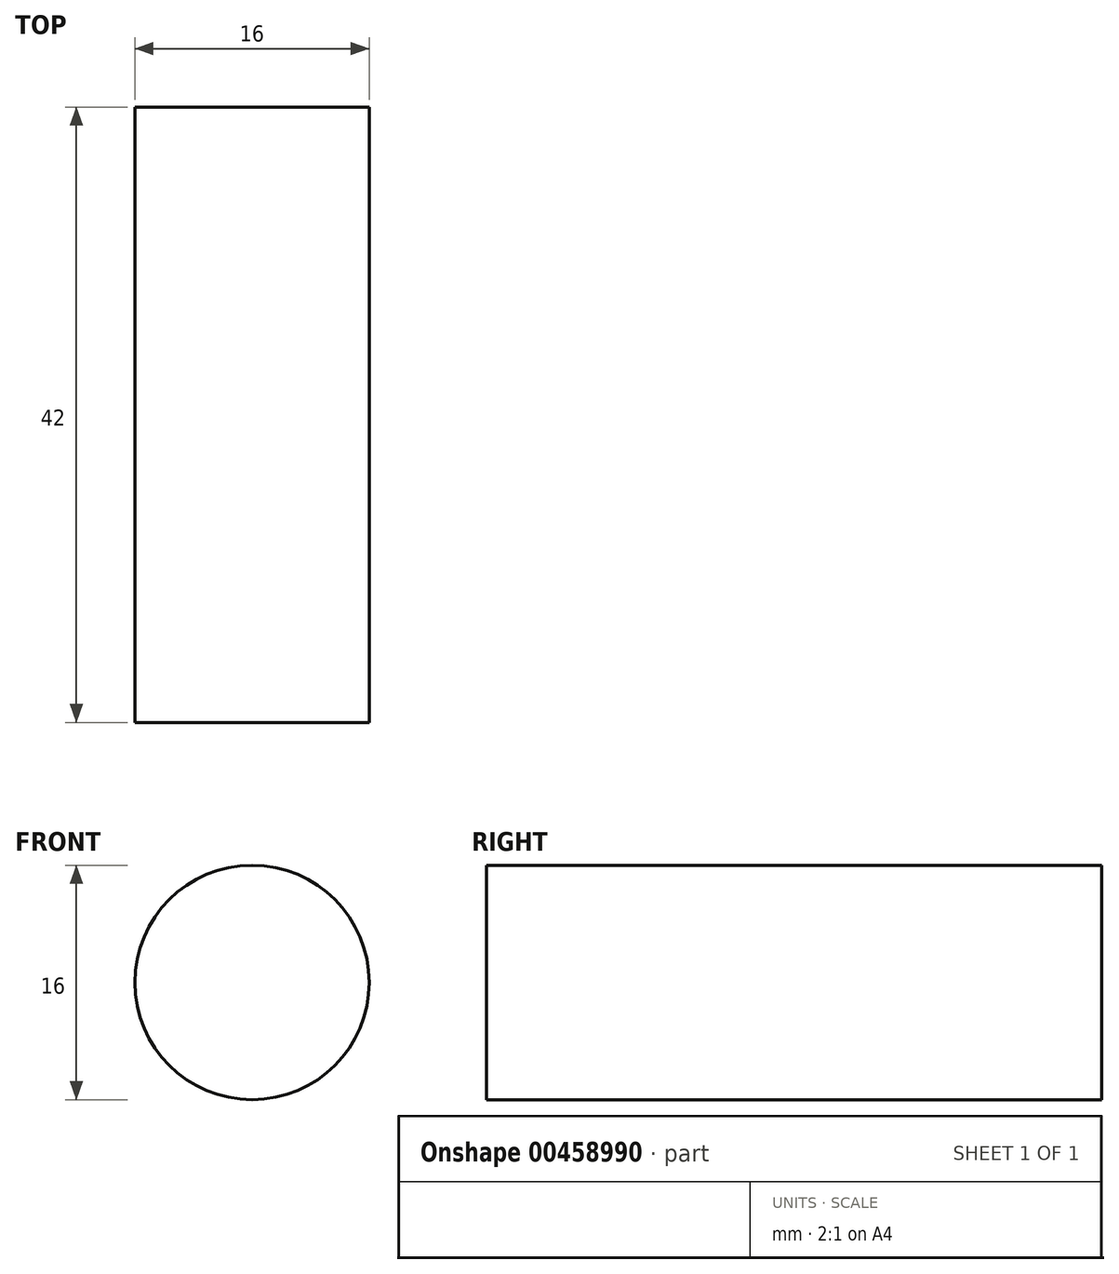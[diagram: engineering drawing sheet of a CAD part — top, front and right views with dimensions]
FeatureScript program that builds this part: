
annotation { "Feature Type Name" : "Feature", "Feature Type Description" : "" }
export const myFeature = defineFeature(function(context is Context, id is Id, definition is map)
    precondition{}
    {
        {
            var Q0;
            Q0=qCreatedBy(makeId("Front.planeOp"),FACE);
            var sketch = newSketch(context, id + "F0", { "sketchPlane" : qUnion([Q0])});
            skCircle(sketch, "E0", {"center": v(0, 0) * mm, "radius": 8 * mm});
            skSolve(sketch);
        }
        {
            var Q0;
            Q0 = qSketchRegion(id + "F0", true);
            extrude(context, id + "F1", {"entities" : qUnion([Q0]), "depth" : 42 * mm});
        }
    });
